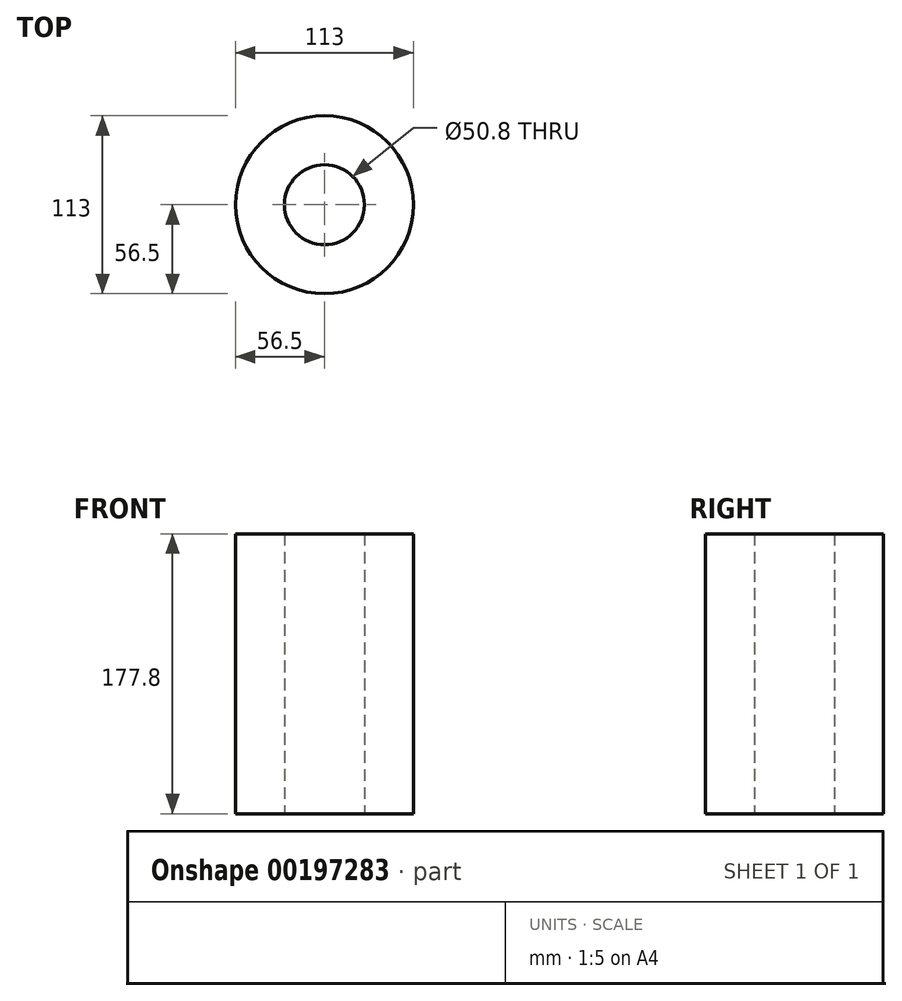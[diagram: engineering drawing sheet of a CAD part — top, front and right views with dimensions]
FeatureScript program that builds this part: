
annotation { "Feature Type Name" : "Feature", "Feature Type Description" : "" }
export const myFeature = defineFeature(function(context is Context, id is Id, definition is map)
    precondition{}
    {
        {
            var Q0;
            Q0=qCreatedBy(makeId("Top.planeOp"),FACE);
            var sketch = newSketch(context, id + "F0", { "sketchPlane" : qUnion([Q0])});
            skCircle(sketch, "E0", {"center": v(0, 0) * mm, "radius": 56.5 * mm});
            skCircle(sketch, "E1", {"center": v(0, 0) * mm, "radius": 25.4 * mm});
            skSolve(sketch);
        }
        {
            var Q0;
            Q0 = qSketchRegion(id + "F0", true);
            extrude(context, id + "F1", {"entities" : qUnion([Q0]), "depth" : 177.8 * mm});
        }
    });
